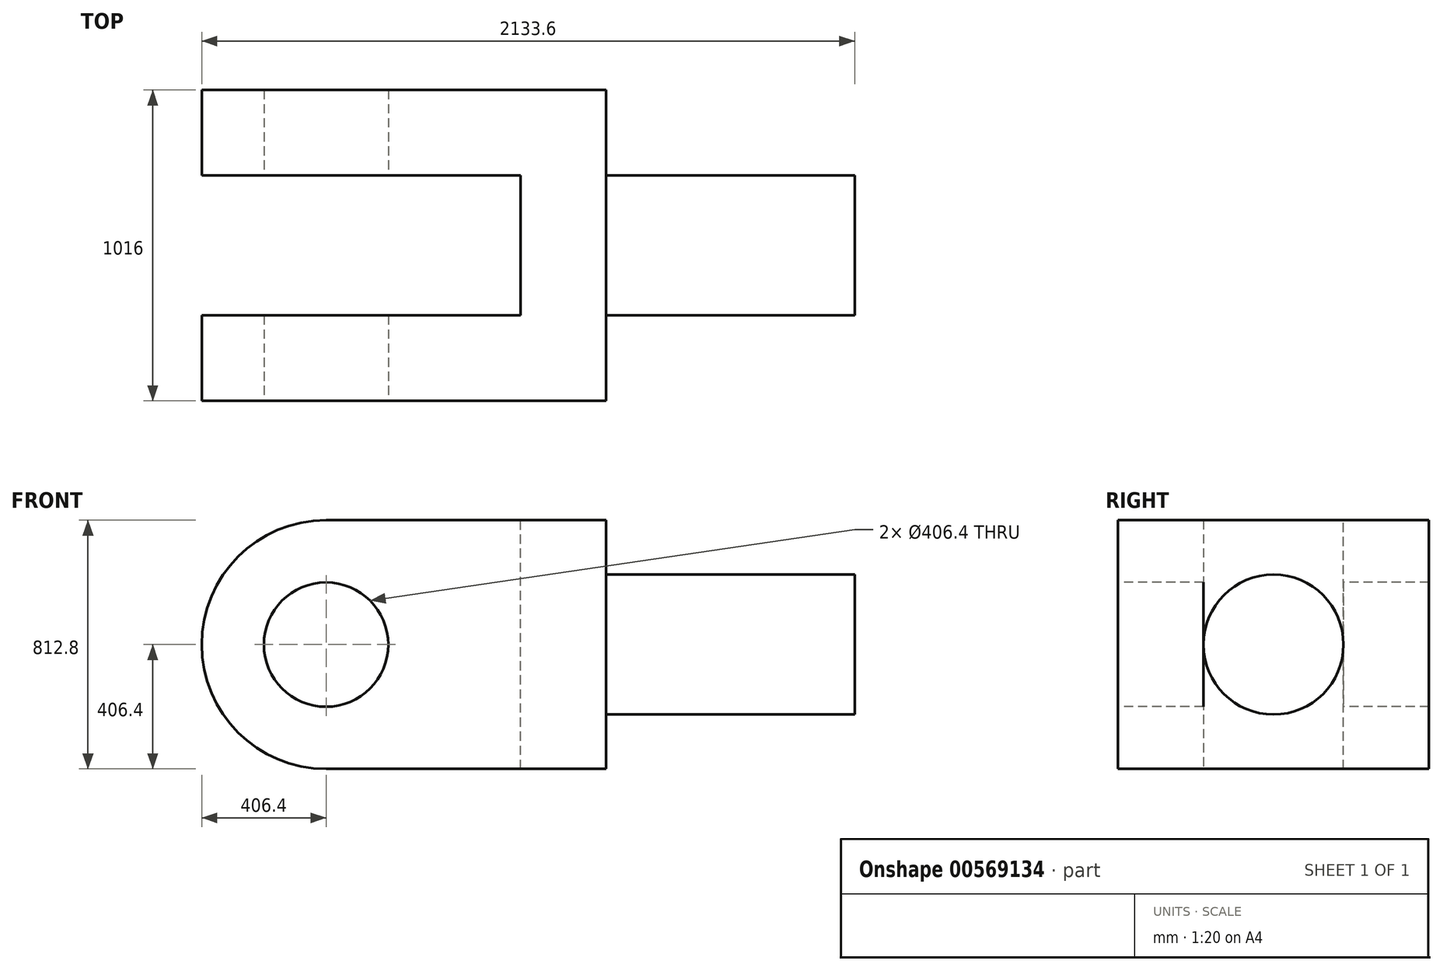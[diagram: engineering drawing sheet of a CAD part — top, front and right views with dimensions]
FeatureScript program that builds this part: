
annotation { "Feature Type Name" : "Feature", "Feature Type Description" : "" }
export const myFeature = defineFeature(function(context is Context, id is Id, definition is map)
    precondition{}
    {
        {
            var Q0;
            Q0=qCreatedBy(makeId("Top.planeOp"),FACE);
            var sketch = newSketch(context, id + "F0", { "sketchPlane" : qUnion([Q0])});
            skLineSegment(sketch, "E0", {"start": v(-115.6, 51.7) * mm, "end": v(1205.2, 51.7) * mm});
            skLineSegment(sketch, "E1", {"start": v(1205.2, 51.7) * mm, "end": v(1205.2, -964.3) * mm});
            skLineSegment(sketch, "E2", {"start": v(1205.2, -964.3) * mm, "end": v(-115.6, -964.3) * mm});
            skLineSegment(sketch, "E3", {"start": v(-115.6, -964.3) * mm, "end": v(-115.6, -684.9) * mm});
            skLineSegment(sketch, "E4", {"start": v(-115.6, -684.9) * mm, "end": v(925.8, -684.9) * mm});
            skLineSegment(sketch, "E5", {"start": v(925.8, -684.9) * mm, "end": v(925.8, -227.7) * mm});
            skLineSegment(sketch, "E6", {"start": v(925.8, -227.7) * mm, "end": v(-115.6, -227.7) * mm});
            skLineSegment(sketch, "E7", {"start": v(-115.6, -227.7) * mm, "end": v(-115.6, 51.7) * mm});
            skLineSegment(sketch, "E8", {"start": v(1205.2, 51.7) * mm, "end": v(1205.2, -227.7) * mm});
            skSolve(sketch);
        }
        {
            var Q0;
            Q0 = qSketchRegion(id + "F0", true);
            extrude(context, id + "F1", {"entities" : qUnion([Q0]), "oppositeDirection" : true, "depth" : 812.8 * mm, "offsetDistance" : 25.4 * mm});
        }
        {
            var Q0;
            Q0=makeQuery(id+"F1.opExtrude","SWEPT_FACE",FACE,{"disambiguationData":[OSD([sQuery(id+"F0.wireOp",EDGE,"E2")])]});
            var sketch = newSketch(context, id + "F2", { "sketchPlane" : qUnion([Q0])});
            skLineSegment(sketch, "E9", {"start": v(1205.2, 0) * mm, "end": v(290.8, 0) * mm});
            skLineSegment(sketch, "E10", {"start": v(290.8, 0) * mm, "end": v(290.8, -406.4) * mm});
            skCircle(sketch, "E11", {"center": v(290.8, -406.4) * mm, "radius": 203.2 * mm});
            skSolve(sketch);
        }
        {
            var Q0;
            Q0=makeQuery(id+"F2.imprint","IMPRINT",FACE,{"disambiguationData":[TD([[makeQuery(id+"F2.imprint","IMPRINT",EDGE,{"derivedFrom":sQuery(id+"F2.wireOp",EDGE,"E11")}),1.0]])]});
            extrude(context, id + "F3", {"entities" : qUnion([Q0]), "operationType" : NewBodyOperationType.REMOVE, "endBound" : BoundingType.THROUGH_ALL, "oppositeDirection" : true, "depth" : 25.4 * mm, "offsetDistance" : 25.4 * mm});
        }
        {
            var Q0;
            Q0=makeQuery(id+"F1.opExtrude","CAP_EDGE",EDGE,{"disambiguationData":[OSD([sQuery(id+"F0.wireOp",EDGE,"E7")])],"isStart":true});
            var Q1;
            Q1=makeQuery(id+"F1.opExtrude","CAP_EDGE",EDGE,{"disambiguationData":[OSD([sQuery(id+"F0.wireOp",EDGE,"E3")])],"isStart":true});
            fillet(context, id + "F4", {"entities" : qUnion([Q0, Q1]), "radius" : 406.4 * mm, "tangentPropagation" : true, "allowEdgeOverflow" : false});
        }
        {
            var Q0;
            Q0=makeQuery(id+"F1.opExtrude","CAP_EDGE",EDGE,{"disambiguationData":[OSD([sQuery(id+"F0.wireOp",EDGE,"E7")])],"isStart":false});
            var Q1;
            Q1=makeQuery(id+"F1.opExtrude","CAP_EDGE",EDGE,{"disambiguationData":[OSD([sQuery(id+"F0.wireOp",EDGE,"E3")])],"isStart":false});
            fillet(context, id + "F5", {"entities" : qUnion([Q0, Q1]), "radius" : 406.4 * mm, "tangentPropagation" : true, "allowEdgeOverflow" : false});
        }
        {
            var Q0;
            Q0=makeQuery(id+"F1.opExtrude","SWEPT_FACE",FACE,{"disambiguationData":[OSD([sQuery(id+"F0.wireOp",EDGE,"E1"),sQuery(id+"F0.wireOp",EDGE,"E8")])]});
            var sketch = newSketch(context, id + "F6", { "sketchPlane" : qUnion([Q0])});
            skLineSegment(sketch, "E12", {"start": v(51.7, 0) * mm, "end": v(-456.3, 0) * mm});
            skLineSegment(sketch, "E13", {"start": v(-456.3, 0) * mm, "end": v(-456.3, -406.4) * mm});
            skCircle(sketch, "E14", {"center": v(-456.3, -406.4) * mm, "radius": 228.6 * mm});
            skSolve(sketch);
        }
        {
            var Q0;
            Q0=makeQuery(id+"F6.imprint","IMPRINT",FACE,{"disambiguationData":[TD([[makeQuery(id+"F6.imprint","IMPRINT",EDGE,{"derivedFrom":sQuery(id+"F6.wireOp",EDGE,"E14")}),1.0]])]});
            extrude(context, id + "F7", {"entities" : qUnion([Q0]), "operationType" : NewBodyOperationType.ADD, "depth" : 812.8 * mm, "offsetDistance" : 25.4 * mm});
        }
    });
